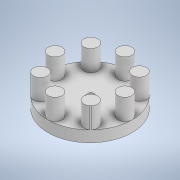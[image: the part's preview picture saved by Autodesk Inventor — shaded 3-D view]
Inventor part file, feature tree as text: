
AUTODESK INVENTOR PART (.ipt)
format: ipt  version: 2022 (Build 260153000, 153)  size: 160,768 bytes
history: native  units: in
note: dims shown in document units (in); Inventor stores cm internally (conversion verified against a paired STEP export)
features: extrude x2, sketch x2
ambient origin geometry x8: Origin, YZ Plane, XZ Plane, XY Plane, X Axis, Y Axis, Z Axis, Center Point
bodies: Solid1 (feature_tree)
feature tree (4):
  extrude  "main shape"  Depth=3.0in
  extrude  "pegs"  Depth=0.75in
  sketch  "Sketch1"  dims[d0=0.2812in d1=3.0in]
  sketch  "Sketch2"  dims[d2=0.1875in d3=0.2454in d4=0.4in d5=0.0in d6=1.0607in d7=1.0607in d8=0.75in d9=0.0in d10=0.5in d11=0.0344in d12=0.5in d13=0.0344in]
